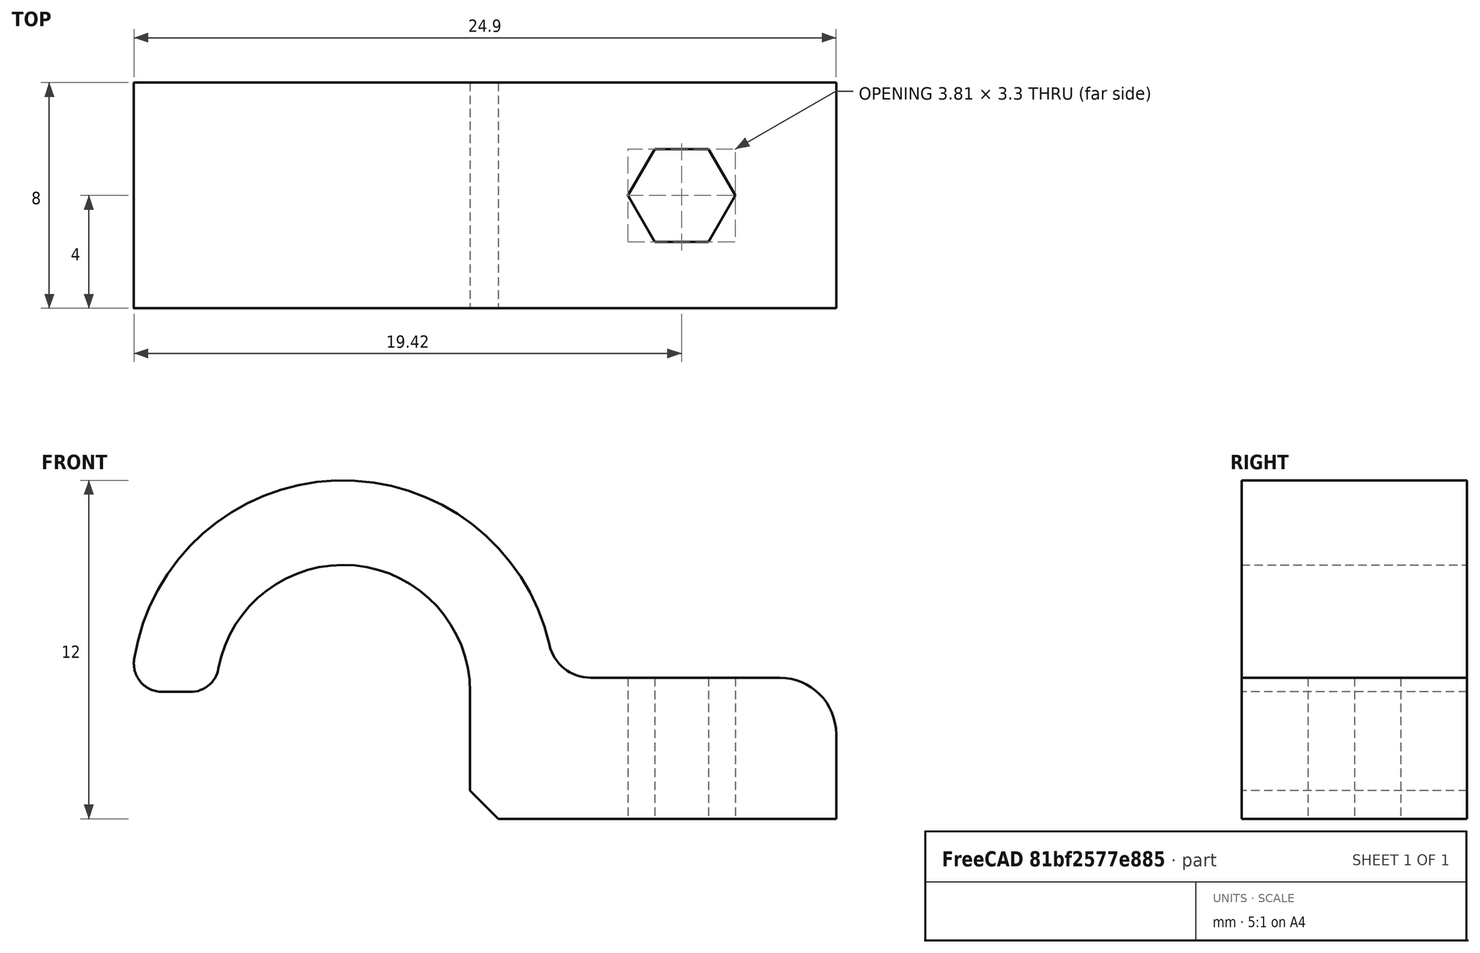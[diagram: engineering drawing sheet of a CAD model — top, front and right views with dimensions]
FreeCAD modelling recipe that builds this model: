
FCSTD DOCUMENT  (FreeCAD 0.19R)
Label: DBWireClips
License: All rights reserved
LicenseURL: http://en.wikipedia.org/wiki/All_rights_reserved
objects: PartDesign::Fillet×4, Sketcher::SketchObject×2, PartDesign::Pad×1, PartDesign::Pocket×1, PartDesign::Chamfer×1, PartDesign::Body×1, Mesh::Feature×1
note: 17 computed .brp shape members not serialized (recipe doc carries the construction recipe); baked Part::Feature solids carry a one-line shape summary decoded from their .brp

FEATURE [Sketcher::SketchObject] Sketch
  FullyConstrained = false
  MapMode = 5
  Placement = pos=(0,0,0) rot=(1,0,0;1.5708rad)
  Support = -> [XZ_Plane]
  sketch-geometry (11):
    g0: ArcOfCircle CenterX=0 CenterY=0 CenterZ=0 NormalX=0 NormalY=0 NormalZ=1 AngleXU=0 Radius=4.5 StartAngle=1e-16 EndAngle=3.14159
    g1: ArcOfCircle CenterX=0 CenterY=0 CenterZ=0 NormalX=0 NormalY=0 NormalZ=1 AngleXU=0 Radius=7.5 StartAngle=0.0667161 EndAngle=3.14159
    g2: LineSegment StartX=4.5 StartY=6e-16 StartZ=0 EndX=4.5 EndY=-4.5 EndZ=0
    g3: LineSegment StartX=4.5 StartY=-4.5 StartZ=0 EndX=17.4833 EndY=-4.5 EndZ=0
    g4: LineSegment StartX=17.4833 StartY=-4.5 StartZ=0 EndX=17.4833 EndY=0.5 EndZ=0
    g5: LineSegment StartX=17.4833 StartY=0.5 StartZ=0 EndX=7.48331 EndY=0.5 EndZ=0
    g6: LineSegment StartX=-7.5 StartY=9e-16 StartZ=0 EndX=-4.5 EndY=9e-16 EndZ=0
    g7: LineSegment StartX=10.6112 StartY=7.66119 StartZ=0 EndX=14.1112 EndY=7.66119 EndZ=0
    g8: LineSegment StartX=14.1112 StartY=7.66119 StartZ=0 EndX=14.1112 EndY=-9.34242 EndZ=0
    g9: LineSegment StartX=14.1112 StartY=-9.34242 StartZ=0 EndX=10.6112 EndY=-9.34242 EndZ=0
    g10: LineSegment StartX=10.6112 StartY=-9.34242 StartZ=0 EndX=10.6112 EndY=7.66119 EndZ=0
  constraints (29):
    c: Coincident(g0,g-1)
    c: Coincident(g1,g0)
    c: Tangent(g0,g2) = 1.5708
    c: Coincident(g2,g3)
    c: Horizontal(g3)
    c: Coincident(g3,g4)
    c: Coincident(g4,g5)
    c: Coincident(g5,g1)
    c: Coincident(g6,g1)
    c: Coincident(g6,g0)
    c: Horizontal(g6)
    c: Vertical(g2)
    c: Diameter(g0) = 9
    c: DistanceY(g2) = -4.5
    c: PointOnObject(g0,g-1)
    c: Horizontal(g5)
    c: Distance(g6) = 3
    c: Vertical(g4)
    c: Coincident(g7,g8)
    c: Coincident(g8,g9)
    c: Coincident(g9,g10)
    c: Coincident(g10,g7)
    c: Horizontal(g7)
    c: Horizontal(g9)
    c: Vertical(g8)
    c: Vertical(g10)
    c: Distance(g7) = 3.5
    c: Distance(g5) = 10
    c: Distance(g4) = 5
FEATURE [PartDesign::Pad] Pad
  Direction = (1,1,1)
  Length = 8
  Length2 = 100
  Placement = pos=(0,0,0) rot=(1,0,0;1.5708rad)
  Profile = -> Sketch
  Type = 0
FEATURE [Sketcher::SketchObject] Sketch001
  FullyConstrained = true
  MapMode = 5
  Placement = pos=(0,3e-16,0.5) rot=(0,0,1;3.14159rad)
  Support = -> [Pad]
  sketch-geometry (7):
    g0: LineSegment StartX=-11.0474 StartY=2.35 StartZ=0 EndX=-10.0947 EndY=4 EndZ=0
    g1: LineSegment StartX=-10.0947 StartY=4 StartZ=0 EndX=-11.0474 EndY=5.65 EndZ=0
    g2: LineSegment StartX=-11.0474 StartY=5.65 StartZ=0 EndX=-12.9526 EndY=5.65 EndZ=0
    g3: LineSegment StartX=-12.9526 StartY=5.65 StartZ=0 EndX=-13.9053 EndY=4 EndZ=0
    g4: LineSegment StartX=-13.9053 StartY=4 StartZ=0 EndX=-12.9526 EndY=2.35 EndZ=0
    g5: LineSegment StartX=-12.9526 StartY=2.35 StartZ=0 EndX=-11.0474 EndY=2.35 EndZ=0
    g6: Circle CenterX=-12 CenterY=4 CenterZ=0 NormalX=0 NormalY=0 NormalZ=1 AngleXU=0 Radius=1.90526
  constraints (17):
    c: Coincident(g0,g1)
    c: Coincident(g1,g2)
    c: Coincident(g2,g3)
    c: Coincident(g3,g4)
    c: Coincident(g4,g5)
    c: Coincident(g5,g0)
    c: Equal(g0, g1-g5) x5
    c: PointOnObject(g0,g6)
    c: PointOnObject(g1,g6)
    c: PointOnObject(g2,g6)
    c: PointOnObject(g3,g6)
    c: PointOnObject(g4,g6)
    c: PointOnObject(g5,g6)
    c: Distance(g0,g4) = 3.3
    c: DistanceY(g6) = 4
    c: DistanceX(g6) = -12
    c: Horizontal(g5)
FEATURE [PartDesign::Pocket] Pocket
  BaseFeature = -> Pad
  Length = 5
  Length2 = 100
  Placement = pos=(0,0,0) rot=(1,0,0;1.5708rad)
  Profile = -> Sketch001
  Type = 1
FEATURE [PartDesign::Fillet] Fillet
  Base = -> Pocket [Edge39]
  BaseFeature = -> Pocket
  Placement = pos=(0,0,0) rot=(1,0,0;1.5708rad)
  Radius = 1.5
  SupportTransform = false
FEATURE [PartDesign::Fillet] Fillet001
  Base = -> Fillet [Edge16]
  BaseFeature = -> Fillet
  Placement = pos=(0,0,0) rot=(1,0,0;1.5708rad)
  Radius = 2
  SupportTransform = false
FEATURE [PartDesign::Fillet] Fillet002
  Base = -> Fillet001 [Edge25]
  BaseFeature = -> Fillet001
  Placement = pos=(0,0,0) rot=(1,0,0;1.5708rad)
  Radius = 1
  SupportTransform = false
FEATURE [PartDesign::Fillet] Fillet003
  Base = -> Fillet002 [Edge18]
  BaseFeature = -> Fillet002
  Placement = pos=(0,0,0) rot=(1,0,0;1.5708rad)
  Radius = 1
  SupportTransform = false
FEATURE [PartDesign::Chamfer] Chamfer
  Angle = 45
  Base = -> Fillet003 [Edge23]
  BaseFeature = -> Fillet003
  ChamferType = 0
  FlipDirection = false
  Placement = pos=(0,0,0) rot=(1,0,0;1.5708rad)
  Size = 1
  Size2 = 1
  SupportTransform = false
FEATURE [PartDesign::Body] Body
  Group = -> [Sketch,Pad,Sketch001,Pocket,Fillet,Fillet001,Fillet002,Fillet003,Chamfer]
  Origin = -> Origin
  Tip = -> Chamfer
FEATURE [Mesh::Feature] Mesh  label="Chamfer (Meshed)"
